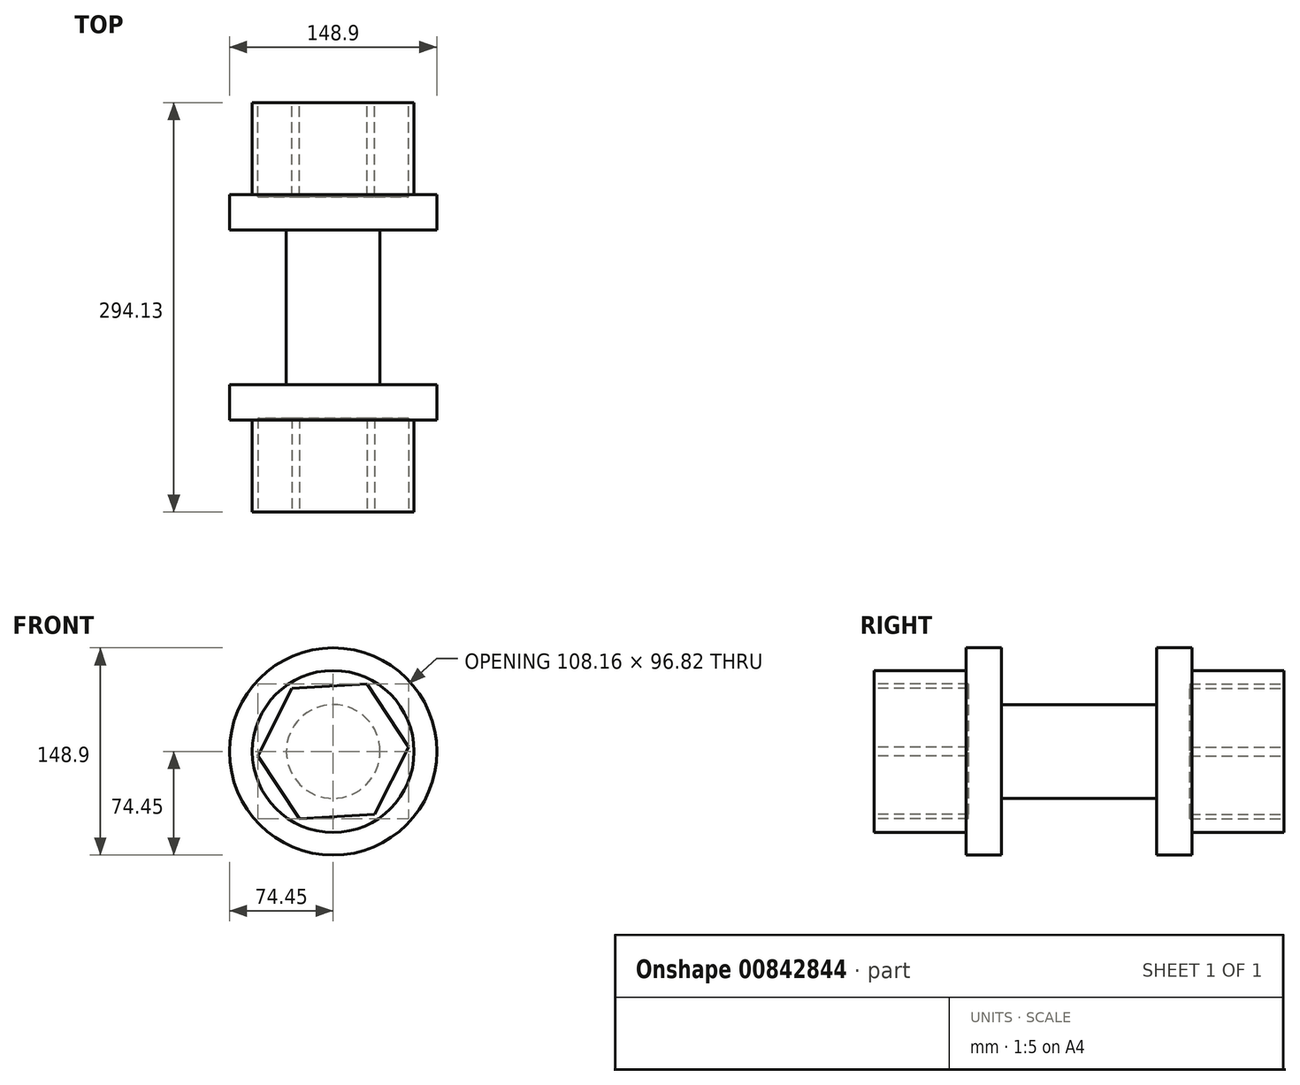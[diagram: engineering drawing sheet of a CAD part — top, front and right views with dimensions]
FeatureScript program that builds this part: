
annotation { "Feature Type Name" : "Feature", "Feature Type Description" : "" }
export const myFeature = defineFeature(function(context is Context, id is Id, definition is map)
    precondition{}
    {
        {
            var Q0;
            Q0=qCreatedBy(makeId("Front.planeOp"),FACE);
            var sketch = newSketch(context, id + "F0", { "sketchPlane" : qUnion([Q0])});
            skCircle(sketch, "E0", {"center": v(0, 0) * mm, "radius": 74.45 * mm});
            skSolve(sketch);
        }
        {
            var Q0;
            Q0=makeQuery(id+"F0.imprint","IMPRINT",FACE,{"disambiguationData":[TD([[makeQuery(id+"F0.imprint","IMPRINT",EDGE,{"derivedFrom":sQuery(id+"F0.wireOp",EDGE,"E0")}),1.0]])]});
            extrude(context, id + "F1", {"entities" : qUnion([Q0]), "depth" : 25.4 * mm, "offsetDistance" : 25.4 * mm});
        }
        {
            var Q0;
            Q0=makeQuery(id+"F1.opExtrude","CAP_FACE",FACE,{"disambiguationData":[OSD([sQuery(id+"F0.wireOp",EDGE,"E0")])],"isStart":true});
            var sketch = newSketch(context, id + "F2", { "sketchPlane" : qUnion([Q0])});
            skCircle(sketch, "E1", {"center": v(0, 0) * mm, "radius": 58.13 * mm});
            skSolve(sketch);
        }
        {
            var Q0;
            Q0=makeQuery(id+"F2.imprint","IMPRINT",FACE,{"disambiguationData":[TD([[makeQuery(id+"F2.imprint","IMPRINT",EDGE,{"derivedFrom":sQuery(id+"F2.wireOp",EDGE,"E1")}),1.0]])]});
            var Q1;
            Q1=sQuery(id+"F2.wireOp",EDGE,"E1");
            extrude(context, id + "F3", {"entities" : qUnion([Q0]), "operationType" : NewBodyOperationType.ADD, "surfaceEntities" : qUnion([Q1]), "depth" : 66.04 * mm, "offsetDistance" : 25.4 * mm});
        }
        {
            var Q0;
            Q0=makeQuery(id+"F3.opExtrude","CAP_FACE",FACE,{"disambiguationData":[OSD([sQuery(id+"F2.wireOp",EDGE,"E1")])],"isStart":false});
            var sketch = newSketch(context, id + "F4", { "sketchPlane" : qUnion([Q0])});
            skCircle(sketch, "E2.cCircle", {"center": v(0, 0) * mm, "radius": 46.92 * mm, "construction": true});
            skLineSegment(sketch, "E2.0", {"start": v(54.08, -3.15) * mm, "end": v(24.32, -48.4) * mm});
            skLineSegment(sketch, "E2.1", {"start": v(24.32, -48.4) * mm, "end": v(-29.77, -45.26) * mm});
            skLineSegment(sketch, "E2.2", {"start": v(-29.77, -45.26) * mm, "end": v(-54.08, 3.15) * mm});
            skLineSegment(sketch, "E2.3", {"start": v(-54.08, 3.15) * mm, "end": v(-24.32, 48.4) * mm});
            skLineSegment(sketch, "E2.4", {"start": v(-24.32, 48.4) * mm, "end": v(29.77, 45.26) * mm});
            skLineSegment(sketch, "E2.5", {"start": v(29.77, 45.26) * mm, "end": v(54.08, -3.15) * mm});
            skPoint(sketch, "E2.0.midPoint", {"position": v(39.2, -25.78) * mm});
            skSolve(sketch);
        }
        {
            var Q0;
            Q0=makeQuery(id+"F4.imprint","IMPRINT",FACE,{"disambiguationData":[TD([[makeQuery(id+"F4.imprint","IMPRINT",EDGE,{"derivedFrom":sQuery(id+"F4.wireOp",EDGE,"E2.0")}),-1.0]])]});
            extrude(context, id + "F5", {"entities" : qUnion([Q0]), "operationType" : NewBodyOperationType.REMOVE, "oppositeDirection" : true, "depth" : 67.56 * mm, "offsetDistance" : 25.4 * mm});
        }
        {
            var Q0;
            Q0=makeQuery(id+"F1.opExtrude","CAP_FACE",FACE,{"disambiguationData":[OSD([sQuery(id+"F0.wireOp",EDGE,"E0")])],"isStart":false});
            var sketch = newSketch(context, id + "F6", { "sketchPlane" : qUnion([Q0])});
            skCircle(sketch, "E3", {"center": v(0, 0) * mm, "radius": 33.67 * mm});
            skSolve(sketch);
        }
        {
            var Q0;
            Q0=makeQuery(id+"F6.imprint","IMPRINT",FACE,{"disambiguationData":[TD([[makeQuery(id+"F6.imprint","IMPRINT",EDGE,{"derivedFrom":sQuery(id+"F6.wireOp",EDGE,"E3")}),1.0]])]});
            extrude(context, id + "F7", {"entities" : qUnion([Q0]), "operationType" : NewBodyOperationType.ADD, "depth" : 55.63 * mm, "offsetDistance" : 25.4 * mm});
        }
        {
            var Q0;
            Q0=makeQuery(id+"F3.opExtrude","SWEPT_BODY",BODY,{"disambiguationData":[OSD([sQuery(id+"F2.wireOp",EDGE,"E1")])]});
            var Q1;
            Q1=makeQuery(id+"F1.opExtrude","SWEPT_BODY",BODY,{"disambiguationData":[OSD([sQuery(id+"F0.wireOp",EDGE,"E0")])]});
            var Q2;
            Q2=makeQuery(id+"F7.opExtrude","CAP_FACE",FACE,{"disambiguationData":[OSD([sQuery(id+"F6.wireOp",EDGE,"E3")])],"isStart":false});
            mirror(context, id + "F8", {"operationType" : NewBodyOperationType.ADD, "entities" : qUnion([Q0, Q1]), "mirrorPlane" : qUnion([Q2])});
        }
    });
